# Revit family: ewf_ewg_ewh_ewj-20_105a_b_y_sa2_ta(40a)2(-60)_60Hz
name_source: partatom
category: 機械設備
units: mm (PartAtom-declared; Revit-internal decimal feet)

## family parameters
OmniClass タイトル = Industrial Ventilating Equipment
OmniClass 番号 = 23.75.35.21.17
パーツ タイプ = 標準
ロード時にボイドで切り取り = はい
丸型コネクタ寸法 = 直径を使用
作業面ベース = いいえ
共有 = いいえ
常に垂直 = はい
部屋計算ポイント = はい

## types (68) — shared parameters
IfcExportAs = IfcFanType
IfcExportType = TUBEAXIAL
MID風量 = 0.0 m³/h
MIN風量 = 0.0 m³/h
OmniClassCode = 23-33 31 19 11 17
URL = https://www.mitsubishielectric.co.jp
Uniclass2015Code = Pr_65_67_29_67
Uniclass2015Title = Propeller fans
Uniclass2015Version = Systems v1.9
ファンの種類 = 軸流羽根
仕様書バージョン = Version1.0
企業コード = 108420
分類コード = 50052503100110
周波数 = 60 Hz
呼称 = 有圧扇
法定耐用年数 = 15
製品リリース年月 = 2022年6月1日
製品出荷対象 = 国内
製造元 = 三菱電機株式会社
設置方法 = 壁付
説明 = 産業用有圧換気扇 低騒音形 排気専用
負荷分類 = 3_ファン類
運転質量 = 0.00 kg

## per-type parameters (varying)
- EWF-20YSA2: Depth=197; Height=320; MAX風量=780.0 m³/h; Width=320; オリフィス_Depth=60  [stored 0.19685 ft]; オリフィス径=249; フレームの厚さ=10  [stored 0.0328084 ft]; モデル=EWF-20YSA2; モーター径=5  [stored 0.0164042 ft]; モーター表示=いいえ; レグ_Depth=187  [stored 0.613517 ft]; レグ_Height=230  [stored 0.754593 ft]; レグ_Width=230  [stored 0.754593 ft]; 価格=41300 $; 極=4; 極数=2; 消費電力=28 W; 相=1; 羽根径=∅200; 製品質量=3.20 kg; 質量=3.84 kg; 銘板_H=52; 銘板_Height=136; 銘板_Width=103; 銘板表示=はい; 電動機出力=15 W; 電圧=100 V
- EWF-25ASA2: Depth=201  [stored 0.659449 ft]; Height=370; MAX風量=1320.0 m³/h; Width=370; オリフィス_Depth=65  [stored 0.213255 ft]; オリフィス径=310; フレームの厚さ=10  [stored 0.0328084 ft]; モデル=EWF-25ASA2; モーター径=5  [stored 0.0164042 ft]; モーター表示=いいえ; レグ_Depth=185; レグ_Height=280; レグ_Width=280; 価格=44000 $; 極=4; 極数=2; 消費電力=50 W; 相=1; 羽根径=∅250; 製品質量=3.90 kg; 質量=4.68 kg; 銘板_H=60  [stored 0.19685 ft]; 銘板_Height=153  [stored 0.501969 ft]; 銘板_Width=120  [stored 0.393701 ft]; 銘板表示=はい; 電動機出力=25 W; 電圧=100 V
- EWF-30BSA2: Depth=197; Height=420; MAX風量=1980.0 m³/h; Width=420; オリフィス_Depth=69  [stored 0.226378 ft]; オリフィス径=359; フレームの厚さ=10  [stored 0.0328084 ft]; モデル=EWF-30BSA2; モーター径=5  [stored 0.0164042 ft]; モーター表示=いいえ; レグ_Depth=181  [stored 0.593832 ft]; レグ_Height=330; レグ_Width=330; 価格=56400 $; 極=4; 極数=2; 消費電力=65 W; 相=1; 羽根径=∅300; 製品質量=5.70 kg; 質量=6.84 kg; 銘板_H=60  [stored 0.19685 ft]; 銘板_Height=153  [stored 0.501969 ft]; 銘板_Width=120  [stored 0.393701 ft]; 銘板表示=はい; 電動機出力=50 W; 電圧=100 V
- EWF-35CSA2: Depth=208; Height=470; MAX風量=2880.0 m³/h; Width=470; オリフィス_Depth=93  [stored 0.305118 ft]; オリフィス径=419; フレームの厚さ=10  [stored 0.0328084 ft]; モデル=EWF-35CSA2; モーター径=5  [stored 0.0164042 ft]; モーター表示=いいえ; レグ_Depth=190; レグ_Height=385; レグ_Width=385; 価格=75000 $; 極=4; 極数=2; 消費電力=113 W; 相=1; 羽根径=∅350; 製品質量=6.60 kg; 質量=7.92 kg; 銘板_H=60  [stored 0.19685 ft]; 銘板_Height=153  [stored 0.501969 ft]; 銘板_Width=120  [stored 0.393701 ft]; 銘板表示=はい; 電動機出力=100 W; 電圧=100 V
- EWF-35DSA2: Depth=259; Height=470; MAX風量=3600.0 m³/h; Width=470; オリフィス_Depth=93  [stored 0.305118 ft]; オリフィス径=419; フレームの厚さ=10  [stored 0.0328084 ft]; モデル=EWF-35DSA2; モーター径=5  [stored 0.0164042 ft]; モーター表示=いいえ; レグ_Depth=227; レグ_Height=385; レグ_Width=385; 価格=82500 $; 極=4; 極数=2; 消費電力=175 W; 相=1; 羽根径=∅350; 製品質量=9.40 kg; 質量=11.28 kg; 銘板_H=73  [stored 0.239501 ft]; 銘板_Height=181  [stored 0.593832 ft]; 銘板_Width=148  [stored 0.485564 ft]; 銘板表示=はい; 電動機出力=150 W; 電圧=100 V
- EWF-40DSA2: Depth=266; Height=520; MAX風量=4320.0 m³/h; Width=520; オリフィス_Depth=99  [stored 0.324803 ft]; オリフィス径=480; フレームの厚さ=10  [stored 0.0328084 ft]; モデル=EWF-40DSA2; モーター径=5  [stored 0.0164042 ft]; モーター表示=いいえ; レグ_Depth=237; レグ_Height=413; レグ_Width=413; 価格=97000 $; 極=4; 極数=2; 消費電力=202 W; 相=1; 羽根径=∅400; 製品質量=12.10 kg; 質量=14.52 kg; 銘板_H=73  [stored 0.239501 ft]; 銘板_Height=181  [stored 0.593832 ft]; 銘板_Width=148  [stored 0.485564 ft]; 銘板表示=はい; 電動機出力=200 W; 電圧=100 V
- EWG-40BSA2: Depth=223  [stored 0.731627 ft]; Height=520; MAX風量=2700.0 m³/h; Width=520; オリフィス_Depth=99  [stored 0.324803 ft]; オリフィス径=480; フレームの厚さ=10  [stored 0.0328084 ft]; モデル=EWG-40BSA2; モーター径=5  [stored 0.0164042 ft]; モーター表示=いいえ; レグ_Depth=207  [stored 0.679134 ft]; レグ_Height=413; レグ_Width=413; 価格=81100 $; 極=6; 極数=2; 消費電力=70 W; 相=1; 羽根径=∅400; 製品質量=8.40 kg; 質量=10.08 kg; 銘板_H=60  [stored 0.19685 ft]; 銘板_Height=153  [stored 0.501969 ft]; 銘板_Width=120  [stored 0.393701 ft]; 銘板表示=はい; 電動機出力=50 W; 電圧=100 V
- EWG-40CSA2: Depth=285; Height=520; MAX風量=3780.0 m³/h; Width=520; オリフィス_Depth=99  [stored 0.324803 ft]; オリフィス径=480; フレームの厚さ=10  [stored 0.0328084 ft]; モデル=EWG-40CSA2; モーター径=5  [stored 0.0164042 ft]; モーター表示=いいえ; レグ_Depth=256; レグ_Height=413; レグ_Width=413; 価格=94900 $; 極=6; 極数=2; 消費電力=131 W; 相=1; 羽根径=∅400; 製品質量=12.20 kg; 質量=14.64 kg; 銘板_H=73  [stored 0.239501 ft]; 銘板_Height=181  [stored 0.593832 ft]; 銘板_Width=148  [stored 0.485564 ft]; 銘板表示=はい; 電動機出力=100 W; 電圧=100 V
- EWF-45ESA2: Depth=307; Height=620; MAX風量=6370.0 m³/h; Width=620; オリフィス_Depth=111; オリフィス径=540; フレームの厚さ=10  [stored 0.0328084 ft]; モデル=EWF-45ESA2; モーター径=5  [stored 0.0164042 ft]; モーター表示=いいえ; レグ_Depth=274; レグ_Height=522; レグ_Width=522; 価格=122000 $; 極=4; 極数=2; 消費電力=390 W; 相=1; 羽根径=∅450; 製品質量=19.00 kg; 質量=22.80 kg; 銘板_H=88  [stored 0.288714 ft]; 銘板_Height=211  [stored 0.692257 ft]; 銘板_Width=178  [stored 0.58399 ft]; 銘板表示=はい; 電動機出力=400 W; 電圧=100 V
- EWG-45DSA2: Depth=307; Height=620; MAX風量=5000.0 m³/h; Width=620; オリフィス_Depth=111; オリフィス径=540; フレームの厚さ=10  [stored 0.0328084 ft]; モデル=EWG-45DSA2; モーター径=5  [stored 0.0164042 ft]; モーター表示=いいえ; レグ_Depth=274; レグ_Height=522; レグ_Width=522; 価格=111000 $; 極=6; 極数=2; 消費電力=220 W; 相=1; 羽根径=∅450; 製品質量=17.30 kg; 質量=20.76 kg; 銘板_H=88  [stored 0.288714 ft]; 銘板_Height=211  [stored 0.692257 ft]; 銘板_Width=178  [stored 0.58399 ft]; 銘板表示=はい; 電動機出力=200 W; 電圧=100 V
- EWF-25ATA2_200V: Depth=201  [stored 0.659449 ft]; Height=370; MAX風量=1320.0 m³/h; Width=370; オリフィス_Depth=65  [stored 0.213255 ft]; オリフィス径=310; フレームの厚さ=10  [stored 0.0328084 ft]; モデル=EWF-25ATA2; モーター径=5  [stored 0.0164042 ft]; モーター表示=いいえ; レグ_Depth=185; レグ_Height=280; レグ_Width=280; 価格=44000 $; 極=4; 極数=3; 消費電力=39 W; 相=3; 羽根径=∅250; 製品質量=4.70 kg; 質量=5.64 kg; 銘板_H=60  [stored 0.19685 ft]; 銘板_Height=153  [stored 0.501969 ft]; 銘板_Width=120  [stored 0.393701 ft]; 銘板表示=はい; 電動機出力=25 W; 電圧=200 V
- EWF-30BTA2_200V: Depth=197; Height=420; MAX風量=1980.0 m³/h; Width=420; オリフィス_Depth=69  [stored 0.226378 ft]; オリフィス径=359; フレームの厚さ=10  [stored 0.0328084 ft]; モデル=EWF-30BTA2; モーター径=5  [stored 0.0164042 ft]; モーター表示=いいえ; レグ_Depth=181  [stored 0.593832 ft]; レグ_Height=330; レグ_Width=330; 価格=56400 $; 極=4; 極数=3; 消費電力=64 W; 相=3; 羽根径=∅300; 製品質量=5.70 kg; 質量=6.84 kg; 銘板_H=60  [stored 0.19685 ft]; 銘板_Height=153  [stored 0.501969 ft]; 銘板_Width=120  [stored 0.393701 ft]; 銘板表示=はい; 電動機出力=50 W; 電圧=200 V
- EWF-35CTA2_200V: Depth=208; Height=470; MAX風量=2880.0 m³/h; Width=470; オリフィス_Depth=93  [stored 0.305118 ft]; オリフィス径=419; フレームの厚さ=10  [stored 0.0328084 ft]; モデル=EWF-35CTA2; モーター径=5  [stored 0.0164042 ft]; モーター表示=いいえ; レグ_Depth=190; レグ_Height=385; レグ_Width=385; 価格=75000 $; 極=4; 極数=3; 消費電力=101 W; 相=3; 羽根径=∅350; 製品質量=6.60 kg; 質量=7.92 kg; 銘板_H=60  [stored 0.19685 ft]; 銘板_Height=153  [stored 0.501969 ft]; 銘板_Width=120  [stored 0.393701 ft]; 銘板表示=はい; 電動機出力=100 W; 電圧=200 V
- EWF-35DTA2_200V: Depth=259; Height=470; MAX風量=3600.0 m³/h; Width=470; オリフィス_Depth=93  [stored 0.305118 ft]; オリフィス径=419; フレームの厚さ=10  [stored 0.0328084 ft]; モデル=EWF-35DTA2; モーター径=5  [stored 0.0164042 ft]; モーター表示=いいえ; レグ_Depth=227; レグ_Height=385; レグ_Width=385; 価格=82500 $; 極=4; 極数=3; 消費電力=168 W; 相=3; 羽根径=∅350; 製品質量=9.40 kg; 質量=11.28 kg; 銘板_H=73  [stored 0.239501 ft]; 銘板_Height=181  [stored 0.593832 ft]; 銘板_Width=148  [stored 0.485564 ft]; 銘板表示=はい; 電動機出力=150 W; 電圧=200 V
- EWF-40DTA2_200V: Depth=266; Height=520; MAX風量=4320.0 m³/h; Width=520; オリフィス_Depth=99  [stored 0.324803 ft]; オリフィス径=480; フレームの厚さ=10  [stored 0.0328084 ft]; モデル=EWF-40DTA2; モーター径=5  [stored 0.0164042 ft]; モーター表示=いいえ; レグ_Depth=237; レグ_Height=413; レグ_Width=413; 価格=97000 $; 極=4; 極数=3; 消費電力=188 W; 相=3; 羽根径=∅400; 製品質量=12.30 kg; 質量=14.76 kg; 銘板_H=73  [stored 0.239501 ft]; 銘板_Height=181  [stored 0.593832 ft]; 銘板_Width=148  [stored 0.485564 ft]; 銘板表示=はい; 電動機出力=200 W; 電圧=200 V
- EWF-40ETA2_200V: Depth=291; Height=520; MAX風量=5520.0 m³/h; Width=520; オリフィス_Depth=99  [stored 0.324803 ft]; オリフィス径=480; フレームの厚さ=10  [stored 0.0328084 ft]; モデル=EWF-40ETA2; モーター径=131  [stored 0.42979 ft]; モーター表示=はい; レグ_Depth=262; レグ_Height=413; レグ_Width=413; 価格=106000 $; 極=4; 極数=3; 消費電力=340 W; 相=3; 羽根径=∅400; 製品質量=13.50 kg; 質量=16.20 kg; 銘板_H=5  [stored 0.0164042 ft]; 銘板_Height=5  [stored 0.0164042 ft]; 銘板_Width=5  [stored 0.0164042 ft]; 銘板表示=いいえ; 電動機出力=400 W; 電圧=200 V
- EWG-40BTA2_200V: Depth=223  [stored 0.731627 ft]; Height=520; MAX風量=2460.0 m³/h; Width=520; オリフィス_Depth=99  [stored 0.324803 ft]; オリフィス径=480; フレームの厚さ=10  [stored 0.0328084 ft]; モデル=EWG-40BTA2; モーター径=5  [stored 0.0164042 ft]; モーター表示=いいえ; レグ_Depth=207  [stored 0.679134 ft]; レグ_Height=413; レグ_Width=413; 価格=81100 $; 極=6; 極数=3; 消費電力=67 W; 相=3; 羽根径=∅400; 製品質量=8.10 kg; 質量=9.72 kg; 銘板_H=60  [stored 0.19685 ft]; 銘板_Height=153  [stored 0.501969 ft]; 銘板_Width=120  [stored 0.393701 ft]; 銘板表示=はい; 電動機出力=50 W; 電圧=200 V
- EWG-40CTA2_200V: Depth=280; Height=520; MAX風量=3780.0 m³/h; Width=520; オリフィス_Depth=99  [stored 0.324803 ft]; オリフィス径=480; フレームの厚さ=10  [stored 0.0328084 ft]; モデル=EWG-40CTA2; モーター径=131  [stored 0.42979 ft]; モーター表示=はい; レグ_Depth=251; レグ_Height=413; レグ_Width=413; 価格=94900 $; 極=6; 極数=3; 消費電力=128 W; 相=3; 羽根径=∅400; 製品質量=12.00 kg; 質量=14.40 kg; 銘板_H=5  [stored 0.0164042 ft]; 銘板_Height=5  [stored 0.0164042 ft]; 銘板_Width=5  [stored 0.0164042 ft]; 銘板表示=いいえ; 電動機出力=100 W; 電圧=200 V
- EWF-45ETA2_200V: Depth=315; Height=620; MAX風量=6700.0 m³/h; Width=620; オリフィス_Depth=111; オリフィス径=540; フレームの厚さ=10  [stored 0.0328084 ft]; モデル=EWF-45ETA2; モーター径=131  [stored 0.42979 ft]; モーター表示=はい; レグ_Depth=286; レグ_Height=522; レグ_Width=522; 価格=122000 $; 極=4; 極数=3; 消費電力=390 W; 相=3; 羽根径=∅450; 製品質量=17.30 kg; 質量=20.76 kg; 銘板_H=5  [stored 0.0164042 ft]; 銘板_Height=5  [stored 0.0164042 ft]; 銘板_Width=5  [stored 0.0164042 ft]; 銘板表示=いいえ; 電動機出力=400 W; 電圧=200 V
- EWG-45DTA2_200V: Depth=309; Height=620; MAX風量=5100.0 m³/h; Width=620; オリフィス_Depth=111; オリフィス径=540; フレームの厚さ=10  [stored 0.0328084 ft]; モデル=EWG-45DTA2; モーター径=131  [stored 0.42979 ft]; モーター表示=はい; レグ_Depth=280; レグ_Height=514; レグ_Width=514; 価格=111000 $; 極=6; 極数=3; 消費電力=190 W; 相=3; 羽根径=∅450; 製品質量=15.20 kg; 質量=18.24 kg; 銘板_H=5  [stored 0.0164042 ft]; 銘板_Height=5  [stored 0.0164042 ft]; 銘板_Width=5  [stored 0.0164042 ft]; 銘板表示=いいえ; 電動機出力=200 W; 電圧=200 V
- EWF-25ATA2_220V: Depth=201  [stored 0.659449 ft]; Height=370; MAX風量=1320.0 m³/h; Width=370; オリフィス_Depth=65  [stored 0.213255 ft]; オリフィス径=310; フレームの厚さ=10  [stored 0.0328084 ft]; モデル=EWF-25ATA2; モーター径=5  [stored 0.0164042 ft]; モーター表示=いいえ; レグ_Depth=185; レグ_Height=280; レグ_Width=280; 価格=44000 $; 極=4; 極数=3; 消費電力=45 W; 相=3; 羽根径=∅250; 製品質量=4.70 kg; 質量=5.64 kg; 銘板_H=60  [stored 0.19685 ft]; 銘板_Height=153  [stored 0.501969 ft]; 銘板_Width=120  [stored 0.393701 ft]; 銘板表示=はい; 電動機出力=25 W; 電圧=220 V
- EWF-30BTA2_220V: Depth=197; Height=420; MAX風量=1980.0 m³/h; Width=420; オリフィス_Depth=69  [stored 0.226378 ft]; オリフィス径=359; フレームの厚さ=10  [stored 0.0328084 ft]; モデル=EWF-30BTA2; モーター径=5  [stored 0.0164042 ft]; モーター表示=いいえ; レグ_Depth=181  [stored 0.593832 ft]; レグ_Height=330; レグ_Width=330; 価格=56400 $; 極=4; 極数=3; 消費電力=69 W; 相=3; 羽根径=∅300; 製品質量=5.70 kg; 質量=6.84 kg; 銘板_H=60  [stored 0.19685 ft]; 銘板_Height=153  [stored 0.501969 ft]; 銘板_Width=120  [stored 0.393701 ft]; 銘板表示=はい; 電動機出力=50 W; 電圧=220 V
- EWF-35CTA2_220V: Depth=208; Height=470; MAX風量=2880.0 m³/h; Width=470; オリフィス_Depth=93  [stored 0.305118 ft]; オリフィス径=419; フレームの厚さ=10  [stored 0.0328084 ft]; モデル=EWF-35CTA2; モーター径=5  [stored 0.0164042 ft]; モーター表示=いいえ; レグ_Depth=190; レグ_Height=385; レグ_Width=385; 価格=75000 $; 極=4; 極数=3; 消費電力=112 W; 相=3; 羽根径=∅350; 製品質量=6.60 kg; 質量=7.92 kg; 銘板_H=60  [stored 0.19685 ft]; 銘板_Height=153  [stored 0.501969 ft]; 銘板_Width=120  [stored 0.393701 ft]; 銘板表示=はい; 電動機出力=100 W; 電圧=220 V
- EWF-35DTA2_220V: Depth=259; Height=470; MAX風量=3600.0 m³/h; Width=470; オリフィス_Depth=93  [stored 0.305118 ft]; オリフィス径=419; フレームの厚さ=10  [stored 0.0328084 ft]; モデル=EWF-35DTA2; モーター径=5  [stored 0.0164042 ft]; モーター表示=いいえ; レグ_Depth=227; レグ_Height=385; レグ_Width=385; 価格=82500 $; 極=4; 極数=3; 消費電力=176 W; 相=3; 羽根径=∅350; 製品質量=9.40 kg; 質量=11.28 kg; 銘板_H=73  [stored 0.239501 ft]; 銘板_Height=181  [stored 0.593832 ft]; 銘板_Width=148  [stored 0.485564 ft]; 銘板表示=はい; 電動機出力=150 W; 電圧=220 V
- EWF-40DTA2_220V: Depth=266; Height=520; MAX風量=4320.0 m³/h; Width=520; オリフィス_Depth=99  [stored 0.324803 ft]; オリフィス径=480; フレームの厚さ=10  [stored 0.0328084 ft]; モデル=EWF-40DTA2; モーター径=5  [stored 0.0164042 ft]; モーター表示=いいえ; レグ_Depth=237; レグ_Height=413; レグ_Width=413; 価格=97000 $; 極=4; 極数=3; 消費電力=198 W; 相=3; 羽根径=∅400; 製品質量=12.30 kg; 質量=14.76 kg; 銘板_H=73  [stored 0.239501 ft]; 銘板_Height=181  [stored 0.593832 ft]; 銘板_Width=148  [stored 0.485564 ft]; 銘板表示=はい; 電動機出力=200 W; 電圧=220 V
- EWF-40ETA2_220V: Depth=291; Height=520; MAX風量=5520.0 m³/h; Width=520; オリフィス_Depth=99  [stored 0.324803 ft]; オリフィス径=480; フレームの厚さ=10  [stored 0.0328084 ft]; モデル=EWF-40ETA2; モーター径=131  [stored 0.42979 ft]; モーター表示=はい; レグ_Depth=262; レグ_Height=413; レグ_Width=413; 価格=106000 $; 極=4; 極数=3; 消費電力=350 W; 相=3; 羽根径=∅400; 製品質量=13.50 kg; 質量=16.20 kg; 銘板_H=5  [stored 0.0164042 ft]; 銘板_Height=5  [stored 0.0164042 ft]; 銘板_Width=5  [stored 0.0164042 ft]; 銘板表示=いいえ; 電動機出力=400 W; 電圧=220 V
- EWG-40BTA2_220V: Depth=223  [stored 0.731627 ft]; Height=520; MAX風量=2460.0 m³/h; Width=520; オリフィス_Depth=99  [stored 0.324803 ft]; オリフィス径=480; フレームの厚さ=10  [stored 0.0328084 ft]; モデル=EWG-40BTA2; モーター径=5  [stored 0.0164042 ft]; モーター表示=いいえ; レグ_Depth=207  [stored 0.679134 ft]; レグ_Height=413; レグ_Width=413; 価格=81100 $; 極=6; 極数=3; 消費電力=75 W; 相=3; 羽根径=∅400; 製品質量=8.10 kg; 質量=9.72 kg; 銘板_H=60  [stored 0.19685 ft]; 銘板_Height=153  [stored 0.501969 ft]; 銘板_Width=120  [stored 0.393701 ft]; 銘板表示=はい; 電動機出力=50 W; 電圧=220 V
- EWG-40CTA2_220V: Depth=280; Height=520; MAX風量=3780.0 m³/h; Width=520; オリフィス_Depth=99  [stored 0.324803 ft]; オリフィス径=480; フレームの厚さ=10  [stored 0.0328084 ft]; モデル=EWG-40CTA2; モーター径=131  [stored 0.42979 ft]; モーター表示=はい; レグ_Depth=251; レグ_Height=413; レグ_Width=413; 価格=94900 $; 極=6; 極数=3; 消費電力=136 W; 相=3; 羽根径=∅400; 製品質量=12.00 kg; 質量=14.40 kg; 銘板_H=5  [stored 0.0164042 ft]; 銘板_Height=5  [stored 0.0164042 ft]; 銘板_Width=5  [stored 0.0164042 ft]; 銘板表示=いいえ; 電動機出力=100 W; 電圧=220 V
- EWF-45ETA2_220V: Depth=315; Height=620; MAX風量=6700.0 m³/h; Width=620; オリフィス_Depth=111; オリフィス径=540; フレームの厚さ=10  [stored 0.0328084 ft]; モデル=EWF-45ETA2; モーター径=131  [stored 0.42979 ft]; モーター表示=はい; レグ_Depth=286; レグ_Height=522; レグ_Width=522; 価格=122000 $; 極=4; 極数=3; 消費電力=405 W; 相=3; 羽根径=∅450; 製品質量=17.30 kg; 質量=20.76 kg; 銘板_H=5  [stored 0.0164042 ft]; 銘板_Height=5  [stored 0.0164042 ft]; 銘板_Width=5  [stored 0.0164042 ft]; 銘板表示=いいえ; 電動機出力=400 W; 電圧=220 V
- EWG-45DTA2_220V: Depth=309; Height=620; MAX風量=5100.0 m³/h; Width=620; オリフィス_Depth=111; オリフィス径=540; フレームの厚さ=10  [stored 0.0328084 ft]; モデル=EWG-45DTA2; モーター径=131  [stored 0.42979 ft]; モーター表示=はい; レグ_Depth=280; レグ_Height=514; レグ_Width=514; 価格=111000 $; 極=6; 極数=3; 消費電力=200 W; 相=3; 羽根径=∅450; 製品質量=15.20 kg; 質量=18.24 kg; 銘板_H=5  [stored 0.0164042 ft]; 銘板_Height=5  [stored 0.0164042 ft]; 銘板_Width=5  [stored 0.0164042 ft]; 銘板表示=いいえ; 電動機出力=200 W; 電圧=220 V
- EWF-50FTA2_200V: Depth=295; Height=620; MAX風量=8280.0 m³/h; Width=620; オリフィス_Depth=84  [stored 0.275591 ft]; オリフィス径=590; フレームの厚さ=10  [stored 0.0328084 ft]; モデル=EWF-50FTA2; モーター径=131  [stored 0.42979 ft]; モーター表示=はい; レグ_Depth=266; レグ_Height=522; レグ_Width=522; 価格=134000 $; 極=4; 極数=3; 消費電力=520 W; 相=3; 羽根径=∅500; 製品質量=19.40 kg; 質量=23.28 kg; 銘板_H=5  [stored 0.0164042 ft]; 銘板_Height=5  [stored 0.0164042 ft]; 銘板_Width=5  [stored 0.0164042 ft]; 銘板表示=いいえ; 電動機出力=750 W; 電圧=200 V
- EWG-50DTA2_200V: Depth=295; Height=620; MAX風量=5640.0 m³/h; Width=620; オリフィス_Depth=84  [stored 0.275591 ft]; オリフィス径=590; フレームの厚さ=10  [stored 0.0328084 ft]; モデル=EWG-50DTA2; モーター径=131  [stored 0.42979 ft]; モーター表示=はい; レグ_Depth=266; レグ_Height=514; レグ_Width=514; 価格=108000 $; 極=6; 極数=3; 消費電力=185 W; 相=3; 羽根径=∅500; 製品質量=16.50 kg; 質量=19.80 kg; 銘板_H=5  [stored 0.0164042 ft]; 銘板_Height=5  [stored 0.0164042 ft]; 銘板_Width=5  [stored 0.0164042 ft]; 銘板表示=いいえ; 電動機出力=200 W; 電圧=200 V
- EWG-50ETA2_200V: Depth=315; Height=620; MAX風量=7140.0 m³/h; Width=620; オリフィス_Depth=84  [stored 0.275591 ft]; オリフィス径=590; フレームの厚さ=10  [stored 0.0328084 ft]; モデル=EWG-50ETA2; モーター径=131  [stored 0.42979 ft]; モーター表示=はい; レグ_Depth=286; レグ_Height=514; レグ_Width=514; 価格=125000 $; 極=6; 極数=3; 消費電力=335 W; 相=3; 羽根径=∅500; 製品質量=18.20 kg; 質量=21.84 kg; 銘板_H=5  [stored 0.0164042 ft]; 銘板_Height=5  [stored 0.0164042 ft]; 銘板_Width=5  [stored 0.0164042 ft]; 銘板表示=いいえ; 電動機出力=400 W; 電圧=200 V
- EWF-60HTA2_200V: Depth=313; Height=710; MAX風量=15000.0 m³/h; Width=710; オリフィス_Depth=120  [stored 0.393701 ft]; オリフィス径=703; フレームの厚さ=10  [stored 0.0328084 ft]; モデル=EWF-60HTA2; モーター径=202  [stored 0.66273 ft]; モーター表示=はい; レグ_Depth=228  [stored 0.748031 ft]; レグ_Height=605; レグ_Width=605; 価格=234000 $; 極=4; 極数=3; 消費電力=1080 W; 相=3; 羽根径=∅600; 製品質量=29.00 kg; 質量=34.80 kg; 銘板_H=5  [stored 0.0164042 ft]; 銘板_Height=5  [stored 0.0164042 ft]; 銘板_Width=5  [stored 0.0164042 ft]; 銘板表示=いいえ; 電動機出力=2200 W; 電圧=200 V
- EWG-60ETA2_200V: Depth=291; Height=710; MAX風量=9210.0 m³/h; Width=710; オリフィス_Depth=119  [stored 0.39042 ft]; オリフィス径=703; フレームの厚さ=10  [stored 0.0328084 ft]; モデル=EWG-60ETA2; モーター径=131  [stored 0.42979 ft]; モーター表示=はい; レグ_Depth=262; レグ_Height=604; レグ_Width=604; 価格=139000 $; 極=6; 極数=3; 消費電力=335 W; 相=3; 羽根径=∅600; 製品質量=19.90 kg; 質量=23.88 kg; 銘板_H=5  [stored 0.0164042 ft]; 銘板_Height=5  [stored 0.0164042 ft]; 銘板_Width=5  [stored 0.0164042 ft]; 銘板表示=いいえ; 電動機出力=400 W; 電圧=200 V
- EWG-60FTA2_200V: Depth=347; Height=710; MAX風量=11160.0 m³/h; Width=710; オリフィス_Depth=119  [stored 0.39042 ft]; オリフィス径=703; フレームの厚さ=10  [stored 0.0328084 ft]; モデル=EWG-60FTA2; モーター径=163  [stored 0.534777 ft]; モーター表示=はい; レグ_Depth=309; レグ_Height=612; レグ_Width=612; 価格=165000 $; 極=6; 極数=3; 消費電力=585 W; 相=3; 羽根径=∅600; 製品質量=25.00 kg; 質量=30.00 kg; 銘板_H=5  [stored 0.0164042 ft]; 銘板_Height=5  [stored 0.0164042 ft]; 銘板_Width=5  [stored 0.0164042 ft]; 銘板表示=いいえ; 電動機出力=750 W; 電圧=200 V
- EWF-50FTA2_220V: Depth=295; Height=620; MAX風量=8280.0 m³/h; Width=620; オリフィス_Depth=84  [stored 0.275591 ft]; オリフィス径=590; フレームの厚さ=10  [stored 0.0328084 ft]; モデル=EWF-50FTA2; モーター径=131  [stored 0.42979 ft]; モーター表示=はい; レグ_Depth=266; レグ_Height=522; レグ_Width=522; 価格=134000 $; 極=4; 極数=3; 消費電力=549 W; 相=3; 羽根径=∅500; 製品質量=19.40 kg; 質量=23.28 kg; 銘板_H=5  [stored 0.0164042 ft]; 銘板_Height=5  [stored 0.0164042 ft]; 銘板_Width=5  [stored 0.0164042 ft]; 銘板表示=いいえ; 電動機出力=750 W; 電圧=220 V
- EWG-50DTA2_220V: Depth=295; Height=620; MAX風量=5640.0 m³/h; Width=620; オリフィス_Depth=84  [stored 0.275591 ft]; オリフィス径=590; フレームの厚さ=10  [stored 0.0328084 ft]; モデル=EWG-50DTA2; モーター径=131  [stored 0.42979 ft]; モーター表示=はい; レグ_Depth=266; レグ_Height=514; レグ_Width=514; 価格=108000 $; 極=6; 極数=3; 消費電力=195 W; 相=3; 羽根径=∅500; 製品質量=16.50 kg; 質量=19.80 kg; 銘板_H=5  [stored 0.0164042 ft]; 銘板_Height=5  [stored 0.0164042 ft]; 銘板_Width=5  [stored 0.0164042 ft]; 銘板表示=いいえ; 電動機出力=200 W; 電圧=220 V
- EWG-50ETA2_220V: Depth=315; Height=620; MAX風量=7140.0 m³/h; Width=620; オリフィス_Depth=84  [stored 0.275591 ft]; オリフィス径=590; フレームの厚さ=10  [stored 0.0328084 ft]; モデル=EWG-50ETA2; モーター径=131  [stored 0.42979 ft]; モーター表示=はい; レグ_Depth=286; レグ_Height=514; レグ_Width=514; 価格=125000 $; 極=6; 極数=3; 消費電力=351 W; 相=3; 羽根径=∅500; 製品質量=18.20 kg; 質量=21.84 kg; 銘板_H=5  [stored 0.0164042 ft]; 銘板_Height=5  [stored 0.0164042 ft]; 銘板_Width=5  [stored 0.0164042 ft]; 銘板表示=いいえ; 電動機出力=400 W; 電圧=220 V
- EWF-60HTA2_220V: Depth=313; Height=710; MAX風量=15000.0 m³/h; Width=710; オリフィス_Depth=120  [stored 0.393701 ft]; オリフィス径=703; フレームの厚さ=10  [stored 0.0328084 ft]; モデル=EWF-60HTA2; モーター径=202  [stored 0.66273 ft]; モーター表示=はい; レグ_Depth=228  [stored 0.748031 ft]; レグ_Height=605; レグ_Width=605; 価格=234000 $; 極=4; 極数=3; 消費電力=1100 W; 相=3; 羽根径=∅600; 製品質量=29.00 kg; 質量=34.80 kg; 銘板_H=5  [stored 0.0164042 ft]; 銘板_Height=5  [stored 0.0164042 ft]; 銘板_Width=5  [stored 0.0164042 ft]; 銘板表示=いいえ; 電動機出力=2200 W; 電圧=220 V
- EWG-60ETA2_220V: Depth=291; Height=710; MAX風量=9210.0 m³/h; Width=710; オリフィス_Depth=119  [stored 0.39042 ft]; オリフィス径=703; フレームの厚さ=10  [stored 0.0328084 ft]; モデル=EWG-60ETA2; モーター径=131  [stored 0.42979 ft]; モーター表示=はい; レグ_Depth=262; レグ_Height=604; レグ_Width=604; 価格=139000 $; 極=6; 極数=3; 消費電力=350 W; 相=3; 羽根径=∅600; 製品質量=19.90 kg; 質量=23.88 kg; 銘板_H=5  [stored 0.0164042 ft]; 銘板_Height=5  [stored 0.0164042 ft]; 銘板_Width=5  [stored 0.0164042 ft]; 銘板表示=いいえ; 電動機出力=400 W; 電圧=220 V
- EWG-60FTA2_220V: Depth=347; Height=710; MAX風量=11160.0 m³/h; Width=710; オリフィス_Depth=119  [stored 0.39042 ft]; オリフィス径=703; フレームの厚さ=10  [stored 0.0328084 ft]; モデル=EWG-60FTA2; モーター径=163  [stored 0.534777 ft]; モーター表示=はい; レグ_Depth=309; レグ_Height=612; レグ_Width=612; 価格=165000 $; 極=6; 極数=3; 消費電力=611 W; 相=3; 羽根径=∅600; 製品質量=25.00 kg; 質量=30.00 kg; 銘板_H=5  [stored 0.0164042 ft]; 銘板_Height=5  [stored 0.0164042 ft]; 銘板_Width=5  [stored 0.0164042 ft]; 銘板表示=いいえ; 電動機出力=750 W; 電圧=220 V
- EWG-70JTA2-60_200V: Depth=406; Height=860; MAX風量=23300.0 m³/h; Width=860; オリフィス_Depth=90; オリフィス径=846; フレームの厚さ=35  [stored 0.114829 ft]; モデル=EWG-70JTA2-60; モーター径=289; モーター表示=はい; レグ_Depth=325; レグ_Height=714; レグ_Width=714; 価格=383000 $; 極=6; 極数=3; 消費電力=1980 W; 相=3; 羽根径=∅700; 製品質量=55.00 kg; 質量=66.00 kg; 銘板_H=5  [stored 0.0164042 ft]; 銘板_Height=5  [stored 0.0164042 ft]; 銘板_Width=5  [stored 0.0164042 ft]; 銘板表示=いいえ; 電動機出力=3700 W; 電圧=200 V
- EWG-80LTA2-60_200V: Depth=450; Height=950; MAX風量=32200.0 m³/h; Width=950; オリフィス_Depth=96; オリフィス径=938; フレームの厚さ=35  [stored 0.114829 ft]; モデル=EWG-80LTA2-60; モーター径=289; モーター表示=はい; レグ_Depth=353; レグ_Height=782; レグ_Width=782; 価格=530000 $; 極=6; 極数=3; 消費電力=3390 W; 相=3; 羽根径=∅800; 製品質量=73.00 kg; 質量=87.60 kg; 銘板_H=5  [stored 0.0164042 ft]; 銘板_Height=5  [stored 0.0164042 ft]; 銘板_Width=5  [stored 0.0164042 ft]; 銘板表示=いいえ; 電動機出力=7500 W; 電圧=200 V
- EWH-80JTA2-60_200V: Depth=450; Height=950; MAX風量=24000.0 m³/h; Width=950; オリフィス_Depth=96; オリフィス径=938; フレームの厚さ=35  [stored 0.114829 ft]; モデル=EWH-80JTA2-60; モーター径=231; モーター表示=はい; レグ_Depth=353; レグ_Height=782; レグ_Width=782; 価格=504000 $; 極=8; 極数=3; 消費電力=1540 W; 相=3; 羽根径=∅800; 製品質量=73.00 kg; 質量=87.60 kg; 銘板_H=5  [stored 0.0164042 ft]; 銘板_Height=5  [stored 0.0164042 ft]; 銘板_Width=5  [stored 0.0164042 ft]; 銘板表示=いいえ; 電動機出力=3700 W; 電圧=200 V
- EWH-105MTA2-60_200V: Depth=545; Height=1280; MAX風量=50500.0 m³/h; Width=1280; オリフィス_Depth=200; オリフィス径=1260; フレームの厚さ=50  [stored 0.164042 ft]; モデル=EWH-105MTA2-60; モーター径=305; モーター表示=はい; レグ_Depth=436; レグ_Height=1106; レグ_Width=1106; 価格=985000 $; 極=8; 極数=3; 消費電力=4670 W; 相=3; 羽根径=∅1050; 製品質量=136.00 kg; 質量=163.20 kg; 銘板_H=5  [stored 0.0164042 ft]; 銘板_Height=5  [stored 0.0164042 ft]; 銘板_Width=5  [stored 0.0164042 ft]; 銘板表示=いいえ; 電動機出力=11000 W; 電圧=200 V
- EWJ-105JTA2-60_200V: Depth=545; Height=1280; MAX風量=40600.0 m³/h; Width=1280; オリフィス_Depth=200; オリフィス径=1260; フレームの厚さ=50  [stored 0.164042 ft]; モデル=EWJ-105JTA2-60; モーター径=262; モーター表示=はい; レグ_Depth=424; レグ_Height=1098; レグ_Width=1098; 価格=838000 $; 極=10; 極数=3; 消費電力=2450 W; 相=3; 羽根径=∅1050; 製品質量=130.00 kg; 質量=156.00 kg; 銘板_H=5  [stored 0.0164042 ft]; 銘板_Height=5  [stored 0.0164042 ft]; 銘板_Width=5  [stored 0.0164042 ft]; 銘板表示=いいえ; 電動機出力=3700 W; 電圧=200 V
- EWG-70JTA2-60_220V: Depth=406; Height=860; MAX風量=23300.0 m³/h; Width=860; オリフィス_Depth=90; オリフィス径=846; フレームの厚さ=35  [stored 0.114829 ft]; モデル=EWG-70JTA2-60; モーター径=289; モーター表示=はい; レグ_Depth=325; レグ_Height=714; レグ_Width=714; 価格=383000 $; 極=6; 極数=3; 消費電力=2070 W; 相=3; 羽根径=∅700; 製品質量=55.00 kg; 質量=66.00 kg; 銘板_H=5  [stored 0.0164042 ft]; 銘板_Height=5  [stored 0.0164042 ft]; 銘板_Width=5  [stored 0.0164042 ft]; 銘板表示=いいえ; 電動機出力=3700 W; 電圧=220 V
- EWG-80LTA2-60_220V: Depth=450; Height=950; MAX風量=32200.0 m³/h; Width=950; オリフィス_Depth=96; オリフィス径=938; フレームの厚さ=35  [stored 0.114829 ft]; モデル=EWG-80LTA2-60; モーター径=289; モーター表示=はい; レグ_Depth=353; レグ_Height=782; レグ_Width=782; 価格=530000 $; 極=6; 極数=3; 消費電力=3450 W; 相=3; 羽根径=∅800; 製品質量=73.00 kg; 質量=87.60 kg; 銘板_H=5  [stored 0.0164042 ft]; 銘板_Height=5  [stored 0.0164042 ft]; 銘板_Width=5  [stored 0.0164042 ft]; 銘板表示=いいえ; 電動機出力=7500 W; 電圧=220 V
- EWH-80JTA2-60_220V: Depth=450; Height=950; MAX風量=24000.0 m³/h; Width=950; オリフィス_Depth=96; オリフィス径=938; フレームの厚さ=35  [stored 0.114829 ft]; モデル=EWH-80JTA2-60; モーター径=231; モーター表示=はい; レグ_Depth=353; レグ_Height=782; レグ_Width=782; 価格=504000 $; 極=8; 極数=3; 消費電力=1650 W; 相=3; 羽根径=∅800; 製品質量=73.00 kg; 質量=87.60 kg; 銘板_H=5  [stored 0.0164042 ft]; 銘板_Height=5  [stored 0.0164042 ft]; 銘板_Width=5  [stored 0.0164042 ft]; 銘板表示=いいえ; 電動機出力=3700 W; 電圧=220 V
- EWH-105MTA2-60_220V: Depth=545; Height=1280; MAX風量=50500.0 m³/h; Width=1280; オリフィス_Depth=200; オリフィス径=1260; フレームの厚さ=50  [stored 0.164042 ft]; モデル=EWH-105MTA2-60; モーター径=305; モーター表示=はい; レグ_Depth=436; レグ_Height=1106; レグ_Width=1106; 価格=985000 $; 極=8; 極数=3; 消費電力=4980 W; 相=3; 羽根径=∅1050; 製品質量=136.00 kg; 質量=163.20 kg; 銘板_H=5  [stored 0.0164042 ft]; 銘板_Height=5  [stored 0.0164042 ft]; 銘板_Width=5  [stored 0.0164042 ft]; 銘板表示=いいえ; 電動機出力=11000 W; 電圧=220 V
- EWJ-105JTA2-60_220V: Depth=545; Height=1280; MAX風量=40600.0 m³/h; Width=1280; オリフィス_Depth=200; オリフィス径=1260; フレームの厚さ=50  [stored 0.164042 ft]; モデル=EWJ-105JTA2-60; モーター径=262; モーター表示=はい; レグ_Depth=424; レグ_Height=1098; レグ_Width=1098; 価格=838000 $; 極=10; 極数=3; 消費電力=2480 W; 相=3; 羽根径=∅1050; 製品質量=130.00 kg; 質量=156.00 kg; 銘板_H=5  [stored 0.0164042 ft]; 銘板_Height=5  [stored 0.0164042 ft]; 銘板_Width=5  [stored 0.0164042 ft]; 銘板表示=いいえ; 電動機出力=3700 W; 電圧=220 V
- EWF-25ATA40A2_400V: Depth=201  [stored 0.659449 ft]; Height=370; MAX風量=1320.0 m³/h; Width=370; オリフィス_Depth=65  [stored 0.213255 ft]; オリフィス径=310; フレームの厚さ=10  [stored 0.0328084 ft]; モデル=EWF-25ATA40A2; モーター径=5  [stored 0.0164042 ft]; モーター表示=いいえ; レグ_Depth=185; レグ_Height=280; レグ_Width=280; 価格=48100 $; 極=4; 極数=3; 消費電力=41 W; 相=3; 羽根径=∅250; 製品質量=4.60 kg; 質量=5.52 kg; 銘板_H=60  [stored 0.19685 ft]; 銘板_Height=153  [stored 0.501969 ft]; 銘板_Width=120  [stored 0.393701 ft]; 銘板表示=はい; 電動機出力=25 W; 電圧=400 V
- EWF-30BTA40A2_400V: Depth=197; Height=420; MAX風量=1980.0 m³/h; Width=420; オリフィス_Depth=69  [stored 0.226378 ft]; オリフィス径=359; フレームの厚さ=10  [stored 0.0328084 ft]; モデル=EWF-30BTA40A2; モーター径=5  [stored 0.0164042 ft]; モーター表示=いいえ; レグ_Depth=181  [stored 0.593832 ft]; レグ_Height=330; レグ_Width=330; 価格=62600 $; 極=4; 極数=3; 消費電力=71 W; 相=3; 羽根径=∅300; 製品質量=5.70 kg; 質量=6.84 kg; 銘板_H=60  [stored 0.19685 ft]; 銘板_Height=153  [stored 0.501969 ft]; 銘板_Width=120  [stored 0.393701 ft]; 銘板表示=はい; 電動機出力=50 W; 電圧=400 V
- EWF-35CTA40A2_400V: Depth=208; Height=470; MAX風量=2880.0 m³/h; Width=470; オリフィス_Depth=93  [stored 0.305118 ft]; オリフィス径=419; フレームの厚さ=10  [stored 0.0328084 ft]; モデル=EWF-35CTA40A2; モーター径=5  [stored 0.0164042 ft]; モーター表示=いいえ; レグ_Depth=190; レグ_Height=385; レグ_Width=385; 価格=82500 $; 極=4; 極数=3; 消費電力=106 W; 相=3; 羽根径=∅350; 製品質量=6.60 kg; 質量=7.92 kg; 銘板_H=60  [stored 0.19685 ft]; 銘板_Height=153  [stored 0.501969 ft]; 銘板_Width=120  [stored 0.393701 ft]; 銘板表示=はい; 電動機出力=100 W; 電圧=400 V
- EWF-35DTA40A2_400V: Depth=259; Height=470; MAX風量=3600.0 m³/h; Width=470; オリフィス_Depth=93  [stored 0.305118 ft]; オリフィス径=419; フレームの厚さ=10  [stored 0.0328084 ft]; モデル=EWF-35DTA40A2; モーター径=5  [stored 0.0164042 ft]; モーター表示=いいえ; レグ_Depth=227; レグ_Height=385; レグ_Width=385; 価格=90800 $; 極=4; 極数=3; 消費電力=173 W; 相=3; 羽根径=∅350; 製品質量=9.40 kg; 質量=11.28 kg; 銘板_H=73  [stored 0.239501 ft]; 銘板_Height=181  [stored 0.593832 ft]; 銘板_Width=148  [stored 0.485564 ft]; 銘板表示=はい; 電動機出力=150 W; 電圧=400 V
- EWF-40DTA40A2_400V: Depth=266; Height=520; MAX風量=4320.0 m³/h; Width=520; オリフィス_Depth=99  [stored 0.324803 ft]; オリフィス径=480; フレームの厚さ=10  [stored 0.0328084 ft]; モデル=EWF-40DTA40A2; モーター径=5  [stored 0.0164042 ft]; モーター表示=いいえ; レグ_Depth=237; レグ_Height=413; レグ_Width=413; 価格=105000 $; 極=4; 極数=3; 消費電力=180 W; 相=3; 羽根径=∅400; 製品質量=12.30 kg; 質量=14.76 kg; 銘板_H=73  [stored 0.239501 ft]; 銘板_Height=181  [stored 0.593832 ft]; 銘板_Width=148  [stored 0.485564 ft]; 銘板表示=はい; 電動機出力=200 W; 電圧=400 V
- EWF-40ETA40A2_400V: Depth=291; Height=520; MAX風量=5520.0 m³/h; Width=520; オリフィス_Depth=99  [stored 0.324803 ft]; オリフィス径=480; フレームの厚さ=10  [stored 0.0328084 ft]; モデル=EWF-40ETA40A2; モーター径=131  [stored 0.42979 ft]; モーター表示=はい; レグ_Depth=262; レグ_Height=413; レグ_Width=413; 価格=117000 $; 極=4; 極数=3; 消費電力=340 W; 相=3; 羽根径=∅400; 製品質量=13.50 kg; 質量=16.20 kg; 銘板_H=5  [stored 0.0164042 ft]; 銘板_Height=5  [stored 0.0164042 ft]; 銘板_Width=5  [stored 0.0164042 ft]; 銘板表示=いいえ; 電動機出力=400 W; 電圧=400 V
- EWF-50FTA40A2_400V: Depth=295; Height=620; MAX風量=8280.0 m³/h; Width=620; オリフィス_Depth=84  [stored 0.275591 ft]; オリフィス径=590; フレームの厚さ=10  [stored 0.0328084 ft]; モデル=EWF-50FTA40A2; モーター径=131  [stored 0.42979 ft]; モーター表示=はい; レグ_Depth=266; レグ_Height=522; レグ_Width=522; 価格=146000 $; 極=4; 極数=3; 消費電力=500 W; 相=3; 羽根径=∅500; 製品質量=19.40 kg; 質量=23.28 kg; 銘板_H=5  [stored 0.0164042 ft]; 銘板_Height=5  [stored 0.0164042 ft]; 銘板_Width=5  [stored 0.0164042 ft]; 銘板表示=いいえ; 電動機出力=750 W; 電圧=400 V
- EWG-60FTA40A2_400V: Depth=347; Height=710; MAX風量=11160.0 m³/h; Width=710; オリフィス_Depth=119  [stored 0.39042 ft]; オリフィス径=703; フレームの厚さ=10  [stored 0.0328084 ft]; モデル=EWG-60FTA40A2; モーター径=163  [stored 0.534777 ft]; モーター表示=はい; レグ_Depth=309; レグ_Height=612; レグ_Width=612; 価格=181000 $; 極=6; 極数=3; 消費電力=580 W; 相=3; 羽根径=∅600; 製品質量=25.00 kg; 質量=30.00 kg; 銘板_H=5  [stored 0.0164042 ft]; 銘板_Height=5  [stored 0.0164042 ft]; 銘板_Width=5  [stored 0.0164042 ft]; 銘板表示=いいえ; 電動機出力=750 W; 電圧=400 V
- EWF-25ATA40A2_440V: Depth=201  [stored 0.659449 ft]; Height=370; MAX風量=1320.0 m³/h; Width=370; オリフィス_Depth=65  [stored 0.213255 ft]; オリフィス径=310; フレームの厚さ=10  [stored 0.0328084 ft]; モデル=EWF-25ATA40A2; モーター径=5  [stored 0.0164042 ft]; モーター表示=いいえ; レグ_Depth=185; レグ_Height=280; レグ_Width=280; 価格=48100 $; 極=4; 極数=3; 消費電力=44 W; 相=3; 羽根径=∅250; 製品質量=4.60 kg; 質量=5.52 kg; 銘板_H=60  [stored 0.19685 ft]; 銘板_Height=153  [stored 0.501969 ft]; 銘板_Width=120  [stored 0.393701 ft]; 銘板表示=はい; 電動機出力=25 W; 電圧=440 V
- EWF-30BTA40A2_440V: Depth=197; Height=420; MAX風量=1980.0 m³/h; Width=420; オリフィス_Depth=69  [stored 0.226378 ft]; オリフィス径=359; フレームの厚さ=10  [stored 0.0328084 ft]; モデル=EWF-30BTA40A2; モーター径=5  [stored 0.0164042 ft]; モーター表示=いいえ; レグ_Depth=181  [stored 0.593832 ft]; レグ_Height=330; レグ_Width=330; 価格=62600 $; 極=4; 極数=3; 消費電力=78 W; 相=3; 羽根径=∅300; 製品質量=5.70 kg; 質量=6.84 kg; 銘板_H=60  [stored 0.19685 ft]; 銘板_Height=153  [stored 0.501969 ft]; 銘板_Width=120  [stored 0.393701 ft]; 銘板表示=はい; 電動機出力=50 W; 電圧=440 V
- EWF-35CTA40A2_440V: Depth=208; Height=470; MAX風量=2880.0 m³/h; Width=470; オリフィス_Depth=93  [stored 0.305118 ft]; オリフィス径=419; フレームの厚さ=10  [stored 0.0328084 ft]; モデル=EWF-35CTA40A2; モーター径=5  [stored 0.0164042 ft]; モーター表示=いいえ; レグ_Depth=190; レグ_Height=385; レグ_Width=385; 価格=82500 $; 極=4; 極数=3; 消費電力=114 W; 相=3; 羽根径=∅350; 製品質量=6.60 kg; 質量=7.92 kg; 銘板_H=60  [stored 0.19685 ft]; 銘板_Height=153  [stored 0.501969 ft]; 銘板_Width=120  [stored 0.393701 ft]; 銘板表示=はい; 電動機出力=100 W; 電圧=440 V
- EWF-35DTA40A2_440V: Depth=259; Height=470; MAX風量=3600.0 m³/h; Width=470; オリフィス_Depth=93  [stored 0.305118 ft]; オリフィス径=419; フレームの厚さ=10  [stored 0.0328084 ft]; モデル=EWF-35DTA40A2; モーター径=5  [stored 0.0164042 ft]; モーター表示=いいえ; レグ_Depth=227; レグ_Height=385; レグ_Width=385; 価格=90800 $; 極=4; 極数=3; 消費電力=180 W; 相=3; 羽根径=∅350; 製品質量=9.40 kg; 質量=11.28 kg; 銘板_H=73  [stored 0.239501 ft]; 銘板_Height=181  [stored 0.593832 ft]; 銘板_Width=148  [stored 0.485564 ft]; 銘板表示=はい; 電動機出力=150 W; 電圧=440 V
- EWF-40DTA40A2_440V: Depth=266; Height=520; MAX風量=4320.0 m³/h; Width=520; オリフィス_Depth=99  [stored 0.324803 ft]; オリフィス径=480; フレームの厚さ=10  [stored 0.0328084 ft]; モデル=EWF-40DTA40A2; モーター径=5  [stored 0.0164042 ft]; モーター表示=いいえ; レグ_Depth=237; レグ_Height=413; レグ_Width=413; 価格=105000 $; 極=4; 極数=3; 消費電力=187 W; 相=3; 羽根径=∅400; 製品質量=12.30 kg; 質量=14.76 kg; 銘板_H=73  [stored 0.239501 ft]; 銘板_Height=181  [stored 0.593832 ft]; 銘板_Width=148  [stored 0.485564 ft]; 銘板表示=はい; 電動機出力=200 W; 電圧=440 V
- EWF-40ETA40A2_440V: Depth=291; Height=520; MAX風量=5520.0 m³/h; Width=520; オリフィス_Depth=99  [stored 0.324803 ft]; オリフィス径=480; フレームの厚さ=10  [stored 0.0328084 ft]; モデル=EWF-40ETA40A2; モーター径=131  [stored 0.42979 ft]; モーター表示=はい; レグ_Depth=262; レグ_Height=413; レグ_Width=413; 価格=117000 $; 極=4; 極数=3; 消費電力=340 W; 相=3; 羽根径=∅400; 製品質量=13.50 kg; 質量=16.20 kg; 銘板_H=5  [stored 0.0164042 ft]; 銘板_Height=5  [stored 0.0164042 ft]; 銘板_Width=5  [stored 0.0164042 ft]; 銘板表示=いいえ; 電動機出力=400 W; 電圧=440 V
- EWF-50FTA40A2_440V: Depth=295; Height=620; MAX風量=8280.0 m³/h; Width=620; オリフィス_Depth=84  [stored 0.275591 ft]; オリフィス径=590; フレームの厚さ=10  [stored 0.0328084 ft]; モデル=EWF-50FTA40A2; モーター径=131  [stored 0.42979 ft]; モーター表示=はい; レグ_Depth=266; レグ_Height=522; レグ_Width=522; 価格=146000 $; 極=4; 極数=3; 消費電力=510 W; 相=3; 羽根径=∅500; 製品質量=19.40 kg; 質量=23.28 kg; 銘板_H=5  [stored 0.0164042 ft]; 銘板_Height=5  [stored 0.0164042 ft]; 銘板_Width=5  [stored 0.0164042 ft]; 銘板表示=いいえ; 電動機出力=750 W; 電圧=440 V
- EWG-60FTA40A2_440V: Depth=347; Height=710; MAX風量=11160.0 m³/h; Width=710; オリフィス_Depth=119  [stored 0.39042 ft]; オリフィス径=703; フレームの厚さ=10  [stored 0.0328084 ft]; モデル=EWG-60FTA40A2; モーター径=163  [stored 0.534777 ft]; モーター表示=はい; レグ_Depth=309; レグ_Height=612; レグ_Width=612; 価格=181000 $; 極=6; 極数=3; 消費電力=600 W; 相=3; 羽根径=∅600; 製品質量=25.00 kg; 質量=30.00 kg; 銘板_H=5  [stored 0.0164042 ft]; 銘板_Height=5  [stored 0.0164042 ft]; 銘板_Width=5  [stored 0.0164042 ft]; 銘板表示=いいえ; 電動機出力=750 W; 電圧=440 V

note: [stored X ft] marks values corroborated as IEEE doubles in the binary element streams (Revit-internal decimal feet)
